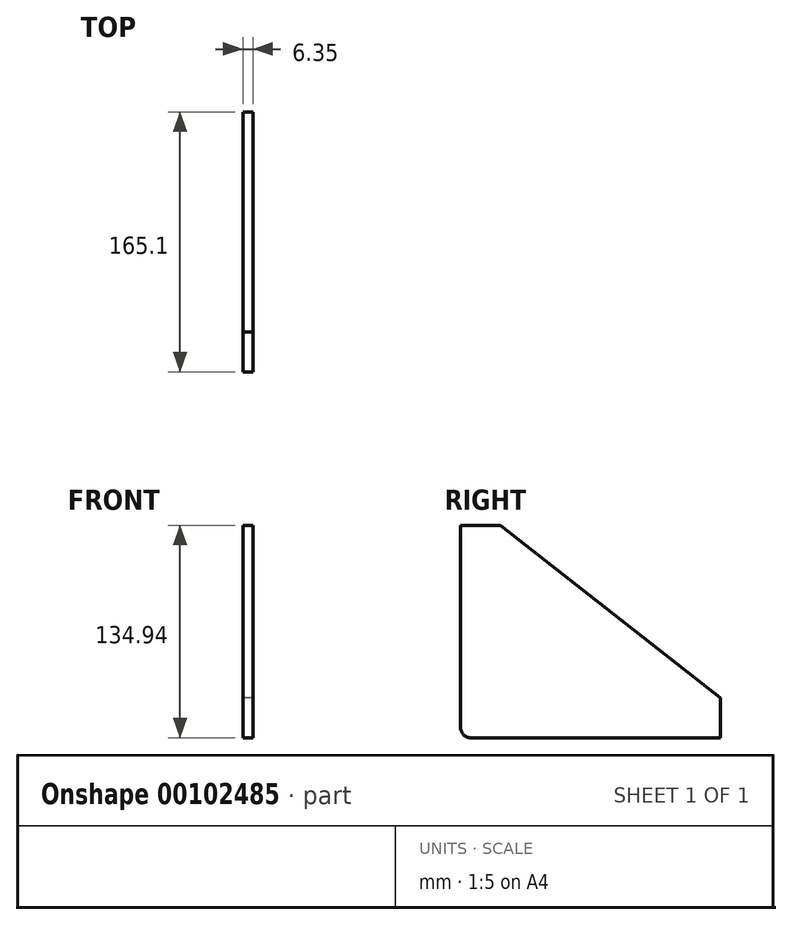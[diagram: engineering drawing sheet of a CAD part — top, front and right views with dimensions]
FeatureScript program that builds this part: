
annotation { "Feature Type Name" : "Feature", "Feature Type Description" : "" }
export const myFeature = defineFeature(function(context is Context, id is Id, definition is map)
    precondition{}
    {
        {
            var Q0;
            Q0=qCreatedBy(makeId("Right.planeOp"),FACE);
            var sketch = newSketch(context, id + "F0", { "sketchPlane" : qUnion([Q0])});
            skLineSegment(sketch, "E0", {"start": v(-82.55, 67.47) * mm, "end": v(-57.15, 67.47) * mm});
            skLineSegment(sketch, "E1", {"start": v(82.55, -67.47) * mm, "end": v(82.55, -42.07) * mm});
            skLineSegment(sketch, "E2", {"start": v(-57.15, 67.47) * mm, "end": v(82.55, -42.07) * mm});
            skLineSegment(sketch, "E3", {"start": v(-82.55, 67.47) * mm, "end": v(-82.55, -61.12) * mm});
            skLineSegment(sketch, "E4", {"start": v(82.55, -67.47) * mm, "end": v(-76.2, -67.47) * mm});
            skArc(sketch, "E5", {"start": v(-82.55, -61.12) * mm, "mid": v(-80.7, -65.6) * mm, "end": v(-76.2, -67.47) * mm});
            skSolve(sketch);
        }
        {
            var Q0;
            Q0 = qSketchRegion(id + "F0", true);
            extrude(context, id + "F1", {"entities" : qUnion([Q0]), "depth" : 6.35 * mm});
        }
    });
